# Revit family: WBC_W_F_1vak Hor_2vak Ver
name_source: partatom
category: Windows
revit_build: Autodesk Revit Architecture 2013 (Build: 20120221_2030(x64)
units: mm (PartAtom-declared; Revit-internal decimal feet)

## types (1)
- WBC_W_F_1vak Hor_2vak Ver
    A = Yes
    Aanzicht Kader 110mm = No
    Aanzicht Kader 68mm = Yes
    Aanzicht Kader 78mm = No
    Aanzicht Kader 88mm = No
    Aanzicht Tussen Regel 110mm = No
    Aanzicht Tussen Regel 150mm = No
    Aanzicht Tussen Regel 200mm = No
    Aanzicht Tussen Regel 68mm = No
    Aanzicht Tussen Regel 78mm = No
    Aanzicht Tussen Regel 88mm = No
    Aanzicht Tussen Stijl 110mm = No
    Aanzicht Tussen Stijl 150mm = No
    Aanzicht Tussen Stijl 200mm = No
    Aanzicht Tussen Stijl 68mm = No
    Aanzicht Tussen Stijl 78mm = Yes
    Aanzicht Tussen Stijl 88mm = No
    Aanzicht Vleugel 35mm = No
    Aanzicht Vleugel 45mm = Yes
    Aanzicht Vleugel 66mm = No
    AanzichtLijnDraai = Yes
    Aanzichtbreedte Kozijn Profielen_68_78_88_110_150mm = 68
    Aanzichtbreedte Raamvleugel Profielen _35_45_66mm = 45
    Aanzichtbreedte Tussen Regels _68_78_88_110_150_200mm = 0
    Aanzichtbreedte Tussen Stijlen _68_78_88_110_150_200mm = 78
    AanzichtlLijnVal = No
    Analytic Construction = <None>
    Assembly Code = B2020110
    B = No
    B1 = 0 mm  [stored 0 ft]
    Beslag Draai = Yes
    Beslag Draai kiep = No
    Beslag Kiep voor draai = No
    Beslag Nen 5096 R.c. 2 = No
    Beslag Nen 5096 R.c. 3 = No
    Beslag Resume 03 = Handgreep A-line (niet afsluitbaar) artikel 276 177
    Beslag Resume 04 = Conform technisch handboek blad LM 4200-D-E
    Beslag Resume 05 = Inbraakwerend draairaambeslag
    Beslag Valraam = No
    Beslag VerborgenScharnieren = No
    Brandwerend volgens: = Nen 6069 criteria Ew30 mits uitgevoerd conform:
    Brandwerend volgens:2 = Rapport 2010-Efectis-R0226[Rev.4] Brandbeoordeling EW 30
    Brandwerendheid = Yes
    Brandwerendheid_old = Yes
    BreedteMaat_1 = 0 mm  [stored 0 ft]
    BreedteMaat_2 = 0 mm  [stored 0 ft]
    BreedteMaat_3 = 0 mm  [stored 0 ft]
    BreedteMaat_4 = 0 mm  [stored 0 ft]
    BreedteMaat_5 = 0 mm  [stored 0 ft]
    C = No
    Cost = 0 $
    D = No
    Default Sill Height = 600 mm
    Description = Kawneer RT 62  volgens:
    Description 2 = Standaard systeemomschrijving RT 62 standaard vlak
    Diepte Versterking Binnenzijde_30_55_75 = 75 mm  [stored 0.246063 ft]
    Diepte Versterking Buitenzijde_30_50_85 = 30 mm  [stored 0.0984252 ft]
    Dikte Stelkozijn = 27 mm  [stored 0.0885827 ft]
    Dikte Stelkozijn onderzijde = 27 mm  [stored 0.0885827 ft]
    DikteStelkozijnOnderzijde_SpelingPui_BuitenbladMWOnderzijde = 17 mm  [stored 0.0557743 ft]
    DikteStelkozijn_SpelingPui_BuitenbladMW = 17 mm  [stored 0.0557743 ft]
    E = No
    F = No
    G = No
    Glasdikte (totaal) = 29 mm  [stored 0.0951444 ft]
    GlassType = Glass, Clear Glazing, Low E
    H = Yes
    HalveSpouw = 65 mm  [stored 0.213255 ft]
    HalveSpouw_OffsetVkKozijn_Stelkozijn = 78 mm  [stored 0.255906 ft]
    Handgreep A_line = Yes
    Handgreep SI_line = No
    Height = 1800 mm  [stored 5.90551 ft]
    Hoogte Tussen regel 1 = 700 mm  [stored 2.29659 ft]
    Hoogte Tussen regel 2 = 0 mm  [stored 0 ft]
    Hoogte Tussen regel 3 = 0 mm  [stored 0 ft]
    Hoogte Tussen regel 4 = 0 mm  [stored 0 ft]
    Hoogte Tussen regel 5 = 0 mm  [stored 0 ft]
    I = Yes
    J = Yes
    Keynote = 30.34
    Kleur Binnenzijde = Kawneer RAL 9010
    Kleur Binnenzijde Vleugel = Kawneer RAL 9010
    Kleur Buitenzijde = Kawneer RAL 9010
    Kleur Buitenzijde Vleugel = Kawneer RAL 9010
    Kleur H&S = Kawneer Anodiseer kleur RVS-look
    Model = NLSfb naam
    NL-SfB-Code = 31.22.22
    OffsetVkKozijnVkStelkozijn = 13 mm  [stored 0.0426509 ft]
    Operation = IfcWindow
    RT 52 = No
    RT 62 = Yes
    RT 72 = No
    ScheduleType |RF| = Aanvulling Description_brandwerend
    Speling Pui_ buitenblad MW = 10 mm  [stored 0.0328084 ft]
    Speling Pui_buitenblad MW Onderzijde = 10 mm  [stored 0.0328084 ft]
    Spouwdiepte = 130 mm  [stored 0.426509 ft]
    Type Comments = Vrij te parameteriseren Revit Model
    URL = http://www.kawneer.com
    Versterking Binnenzijde = Yes
    Versterking Buitenzijde = No
    Wall Closure = By host
    Width = 1200 mm  [stored 3.93701 ft]

note: [stored X ft] marks values corroborated as IEEE doubles in the binary element streams (Revit-internal decimal feet)

## geometry (parser evidence)
native form markers: Blend x22, Sweep x40
no freeform markers — native parametric forms only
